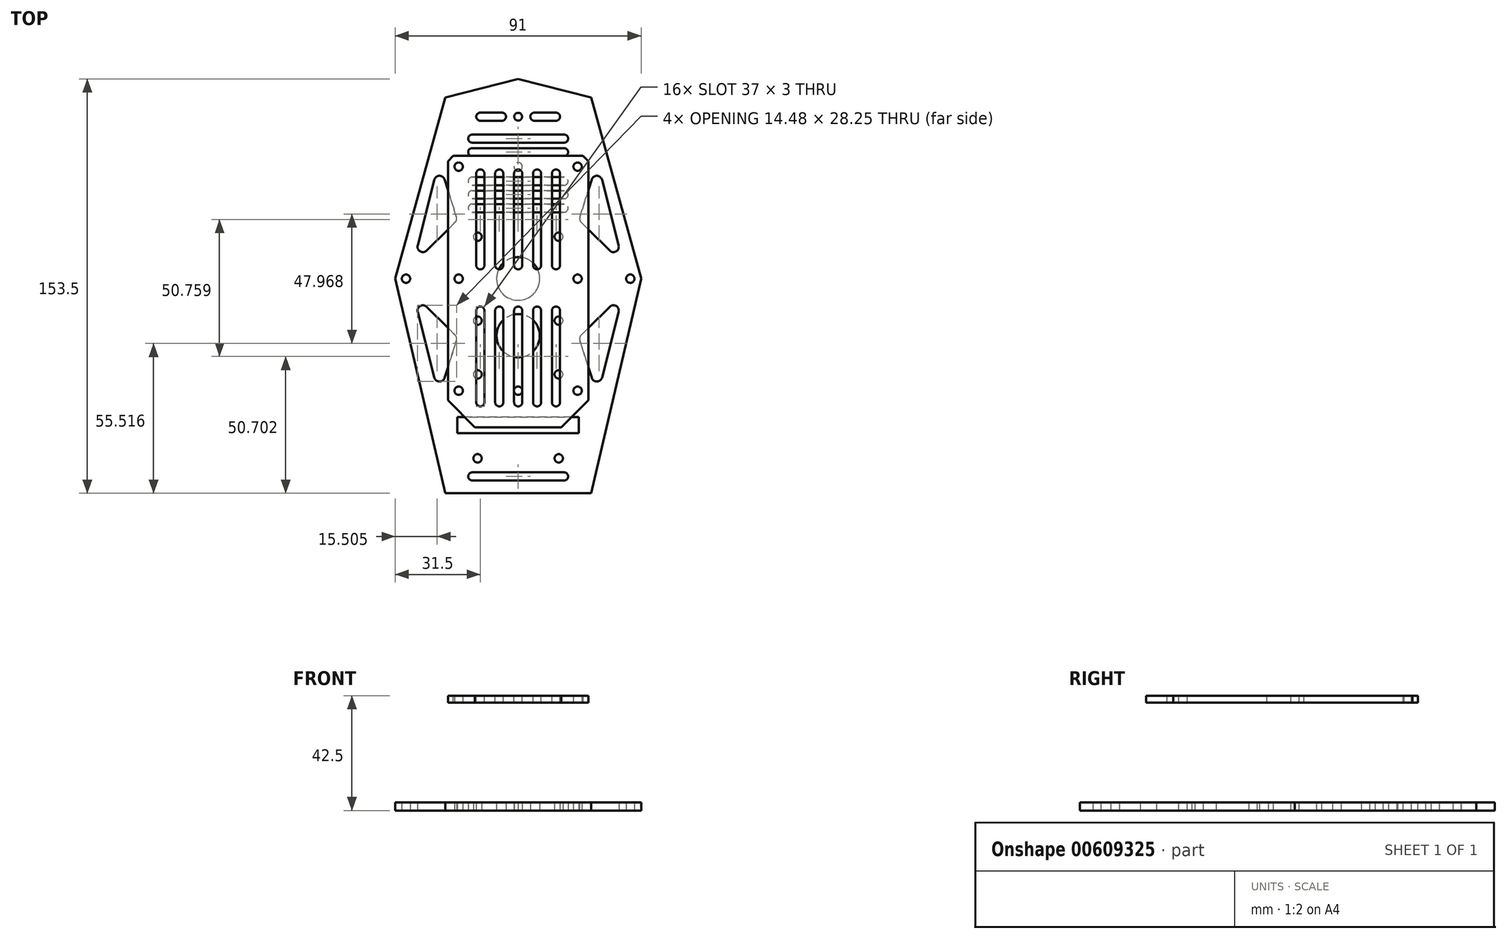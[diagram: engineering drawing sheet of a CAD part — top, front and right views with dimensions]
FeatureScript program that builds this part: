
annotation { "Feature Type Name" : "Feature", "Feature Type Description" : "" }
export const myFeature = defineFeature(function(context is Context, id is Id, definition is map)
    precondition{}
    {
        {
            var Q0;
            Q0=qCreatedBy(makeId("Top.planeOp"),FACE);
            var sketch = newSketch(context, id + "F0", { "sketchPlane" : qUnion([Q0])});
            skLineSegment(sketch, "E0", {"start": v(-27, 60) * mm, "end": v(27, 60) * mm, "construction": true});
            skLineSegment(sketch, "E1.MirrorCS", {"start": v(-27, -60) * mm, "end": v(27, -60) * mm, "construction": true});
            skCircle(sketch, "E2", {"center": v(0, 0) * mm, "radius": 8 * mm});
            skCircle(sketch, "E3", {"center": v(-41.5, 0) * mm, "radius": 1.55 * mm});
            skCircle(sketch, "E4.MirrorC", {"center": v(41.5, 0) * mm, "radius": 1.55 * mm});
            skCircle(sketch, "E5", {"center": v(0, 41.5) * mm, "radius": 1.55 * mm});
            skCircle(sketch, "E6.MirrorC", {"center": v(0, -41.5) * mm, "radius": 1.55 * mm});
            skCircle(sketch, "E7", {"center": v(0, 60) * mm, "radius": 1.46 * mm});
            skLineSegment(sketch, "E8", {"start": v(-6, 60) * mm, "end": v(-6, 61.5) * mm});
            skLineSegment(sketch, "E9", {"start": v(-6, 61.5) * mm, "end": v(-14, 61.5) * mm});
            skLineSegment(sketch, "E10", {"start": v(-14, 61.5) * mm, "end": v(-14, 58.5) * mm});
            skLineSegment(sketch, "E11", {"start": v(-14, 58.5) * mm, "end": v(-6, 58.5) * mm});
            skLineSegment(sketch, "E12", {"start": v(-6, 58.5) * mm, "end": v(-6, 60) * mm});
            skCircle(sketch, "E13", {"center": v(-6, 60) * mm, "radius": 1.5 * mm});
            skCircle(sketch, "E14", {"center": v(-14, 60) * mm, "radius": 1.5 * mm});
            skLineSegment(sketch, "E15.MirrorCS", {"start": v(6, 60) * mm, "end": v(6, 61.5) * mm});
            skLineSegment(sketch, "E16.MirrorCS", {"start": v(6, 58.5) * mm, "end": v(6, 60) * mm});
            skLineSegment(sketch, "E17.MirrorCS", {"start": v(14, 61.5) * mm, "end": v(14, 58.5) * mm});
            skCircle(sketch, "E18.MirrorC", {"center": v(6, 60) * mm, "radius": 1.5 * mm});
            skLineSegment(sketch, "E19.MirrorCS", {"start": v(14, 58.5) * mm, "end": v(6, 58.5) * mm});
            skCircle(sketch, "E20.MirrorC", {"center": v(14, 60) * mm, "radius": 1.5 * mm});
            skLineSegment(sketch, "E21.MirrorCS", {"start": v(6, 61.5) * mm, "end": v(14, 61.5) * mm});
            skSolve(sketch);
        }
        {
            var Q0;
            Q0=qCreatedBy(makeId("Top.planeOp"),FACE);
            var sketch = newSketch(context, id + "F1", { "sketchPlane" : qUnion([Q0])});
            skLineSegment(sketch, "E22.bottom", {"start": v(-18.5, 18.5) * mm, "end": v(18.5, 18.5) * mm, "construction": true});
            skLineSegment(sketch, "E22.top", {"start": v(-18.5, -18.5) * mm, "end": v(18.5, -18.5) * mm, "construction": true});
            skLineSegment(sketch, "E22.left", {"start": v(-18.5, 18.5) * mm, "end": v(-18.5, -18.5) * mm, "construction": true});
            skLineSegment(sketch, "E22.right", {"start": v(18.5, 18.5) * mm, "end": v(18.5, -18.5) * mm, "construction": true});
            skLineSegment(sketch, "E23.bottom", {"start": v(-15.02, 15.55) * mm, "end": v(15.02, 15.55) * mm, "construction": true});
            skLineSegment(sketch, "E23.top", {"start": v(-15.02, -15.55) * mm, "end": v(15.02, -15.55) * mm, "construction": true});
            skLineSegment(sketch, "E23.left", {"start": v(-15.02, 15.55) * mm, "end": v(-15.02, -15.55) * mm, "construction": true});
            skLineSegment(sketch, "E23.right", {"start": v(15.02, 15.55) * mm, "end": v(15.02, -15.55) * mm, "construction": true});
            skPoint(sketch, "E23.middle", {"position": v(0, 0) * mm});
            skCircle(sketch, "E24", {"center": v(-15.02, 15.55) * mm, "radius": 1.55 * mm});
            skCircle(sketch, "E25", {"center": v(-15.02, -15.55) * mm, "radius": 1.55 * mm});
            skCircle(sketch, "E26", {"center": v(15.02, -15.55) * mm, "radius": 1.55 * mm});
            skCircle(sketch, "E27", {"center": v(15.02, 15.55) * mm, "radius": 1.55 * mm});
            skLineSegment(sketch, "E28", {"start": v(0, -18.5) * mm, "end": v(0, -25.5) * mm, "construction": true});
            skLineSegment(sketch, "E29", {"start": v(0, -25.5) * mm, "end": v(18.5, -25.5) * mm, "construction": true});
            skCircle(sketch, "E30.MirrorC", {"center": v(-15.02, -66.55) * mm, "radius": 1.55 * mm});
            skCircle(sketch, "E31.MirrorC", {"center": v(-15.02, -35.45) * mm, "radius": 1.55 * mm});
            skCircle(sketch, "E32.MirrorC", {"center": v(15.02, -66.55) * mm, "radius": 1.55 * mm});
            skCircle(sketch, "E33.MirrorC", {"center": v(15.02, -35.45) * mm, "radius": 1.55 * mm});
            skLineSegment(sketch, "E34.MirrorCS", {"start": v(15.02, -66.55) * mm, "end": v(15.02, -35.45) * mm, "construction": true});
            skLineSegment(sketch, "E35.MirrorCS", {"start": v(-15.02, -66.55) * mm, "end": v(-15.02, -35.45) * mm, "construction": true});
            skLineSegment(sketch, "E36.MirrorCS", {"start": v(-15.02, -35.45) * mm, "end": v(15.02, -35.45) * mm, "construction": true});
            skLineSegment(sketch, "E37.MirrorCS", {"start": v(-15.02, -66.55) * mm, "end": v(15.02, -66.55) * mm, "construction": true});
            skLineSegment(sketch, "E38.MirrorCS", {"start": v(18.5, -69.5) * mm, "end": v(18.5, -32.5) * mm, "construction": true});
            skLineSegment(sketch, "E39.MirrorCS", {"start": v(-18.5, -69.5) * mm, "end": v(-18.5, -32.5) * mm, "construction": true});
            skLineSegment(sketch, "E40.MirrorCS", {"start": v(-18.5, -32.5) * mm, "end": v(18.5, -32.5) * mm, "construction": true});
            skPoint(sketch, "E41.MirrorP", {"position": v(0, -51) * mm});
            skLineSegment(sketch, "E42.MirrorCS", {"start": v(-18.5, -69.5) * mm, "end": v(18.5, -69.5) * mm, "construction": true});
            skLineSegment(sketch, "E43.bottom", {"start": v(-22.5, -57.25) * mm, "end": v(22.5, -57.25) * mm});
            skLineSegment(sketch, "E43.top", {"start": v(-22.5, -51.25) * mm, "end": v(22.5, -51.25) * mm});
            skLineSegment(sketch, "E43.left", {"start": v(-22.5, -57.25) * mm, "end": v(-22.5, -51.25) * mm});
            skLineSegment(sketch, "E43.right", {"start": v(22.5, -57.25) * mm, "end": v(22.5, -51.25) * mm});
            skPoint(sketch, "E43.middle", {"position": v(0, -54.25) * mm});
            skSolve(sketch);
        }
        {
            var Q0;
            Q0=qCreatedBy(makeId("Top.planeOp"),FACE);
            var sketch = newSketch(context, id + "F2", { "sketchPlane" : qUnion([Q0])});
            skLineSegment(sketch, "E44", {"start": v(-27, 67.16) * mm, "end": v(-45.5, 0) * mm});
            skLineSegment(sketch, "E45", {"start": v(-45.5, 0) * mm, "end": v(-27, -79.5) * mm});
            skLineSegment(sketch, "E46", {"start": v(-27, -79.5) * mm, "end": v(0, -79.5) * mm});
            skLineSegment(sketch, "E47.MirrorCS", {"start": v(27, 67.16) * mm, "end": v(45.5, 0) * mm});
            skLineSegment(sketch, "E48.MirrorCS", {"start": v(45.5, 0) * mm, "end": v(27, -79.5) * mm});
            skLineSegment(sketch, "E49.MirrorCS", {"start": v(27, -79.5) * mm, "end": v(0, -79.5) * mm});
            skPoint(sketch, "E50.0", {"position": v(-41.5, 0) * mm});
            skPoint(sketch, "E51.0", {"position": v(0, 60) * mm});
            skLineSegment(sketch, "E52", {"start": v(-27, 67.16) * mm, "end": v(0, 74) * mm});
            skLineSegment(sketch, "E53", {"start": v(0, 74) * mm, "end": v(27, 67.16) * mm});
            skPoint(sketch, "E54.0", {"position": v(0, -69.5) * mm});
            skSolve(sketch);
        }
        {
            var Q0;
            Q0 = qSketchRegion(id + "F2", true);
            extrude(context, id + "F3", {"entities" : qUnion([Q0]), "depth" : 3 * mm, "offsetDistance" : 25 * mm});
        }
        {
            var Q0;
            Q0 = qSketchRegion(id + "F0", true);
            extrude(context, id + "F4", {"entities" : qUnion([Q0]), "operationType" : NewBodyOperationType.REMOVE, "depth" : 25 * mm, "offsetDistance" : 25 * mm, "hasSecondDirection" : true, "secondDirectionOppositeDirection" : true, "secondDirectionDepth" : 25 * mm});
        }
        {
            var Q0;
            Q0 = qSketchRegion(id + "F1", true);
            extrude(context, id + "F5", {"entities" : qUnion([Q0]), "operationType" : NewBodyOperationType.REMOVE, "depth" : 25 * mm, "offsetDistance" : 25 * mm});
        }
        {
            var Q0;
            Q0=qCreatedBy(makeId("Top.planeOp"),FACE);
            var sketch = newSketch(context, id + "F6", { "sketchPlane" : qUnion([Q0])});
            skLineSegment(sketch, "E55", {"start": v(-31.05, -36.6) * mm, "end": v(-37.18, -12.33) * mm});
            skLineSegment(sketch, "E56", {"start": v(-33.83, -10.43) * mm, "end": v(-23.34, -20.85) * mm});
            skLineSegment(sketch, "E57", {"start": v(-22.85, -22.87) * mm, "end": v(-27.2, -36.7) * mm});
            skPoint(sketch, "E58.visualSharp", {"position": v(-38.95, -5.34) * mm});
            skArc(sketch, "E58.filletArc", {"start": v(-33.83, -10.43) * mm, "mid": v(-36.23, -10.1) * mm, "end": v(-37.18, -12.33) * mm});
            skPoint(sketch, "E59.visualSharp", {"position": v(-22.48, -21.7) * mm});
            skArc(sketch, "E59.filletArc", {"start": v(-22.85, -22.87) * mm, "mid": v(-22.81, -21.8) * mm, "end": v(-23.34, -20.85) * mm});
            skPoint(sketch, "E60.visualSharp", {"position": v(-29.32, -43.44) * mm});
            skArc(sketch, "E60.filletArc", {"start": v(-31.05, -36.6) * mm, "mid": v(-29.17, -38.1) * mm, "end": v(-27.2, -36.7) * mm});
            skArc(sketch, "E61.MirrorCS", {"start": v(-22.85, 22.87) * mm, "mid": v(-22.81, 21.8) * mm, "end": v(-23.34, 20.85) * mm});
            skArc(sketch, "E62.MirrorCS", {"start": v(-31.05, 36.6) * mm, "mid": v(-29.17, 38.1) * mm, "end": v(-27.2, 36.7) * mm});
            skArc(sketch, "E63.MirrorCS", {"start": v(-33.83, 10.43) * mm, "mid": v(-36.23, 10.1) * mm, "end": v(-37.18, 12.33) * mm});
            skLineSegment(sketch, "E64.MirrorCS", {"start": v(-33.83, 10.43) * mm, "end": v(-23.34, 20.85) * mm});
            skLineSegment(sketch, "E65.MirrorCS", {"start": v(-22.85, 22.87) * mm, "end": v(-27.2, 36.7) * mm});
            skLineSegment(sketch, "E66.MirrorCS", {"start": v(-31.05, 36.6) * mm, "end": v(-37.18, 12.33) * mm});
            skPoint(sketch, "E67.MirrorP", {"position": v(-22.48, 21.7) * mm});
            skArc(sketch, "E68.MirrorCS", {"start": v(22.85, 22.87) * mm, "mid": v(22.81, 21.8) * mm, "end": v(23.34, 20.85) * mm});
            skArc(sketch, "E69.MirrorCS", {"start": v(31.05, 36.6) * mm, "mid": v(29.17, 38.1) * mm, "end": v(27.2, 36.7) * mm});
            skLineSegment(sketch, "E70.MirrorCS", {"start": v(31.05, 36.6) * mm, "end": v(37.18, 12.33) * mm});
            skArc(sketch, "E71.MirrorCS", {"start": v(33.83, 10.43) * mm, "mid": v(36.23, 10.1) * mm, "end": v(37.18, 12.33) * mm});
            skLineSegment(sketch, "E72.MirrorCS", {"start": v(33.83, 10.43) * mm, "end": v(23.34, 20.85) * mm});
            skLineSegment(sketch, "E73.MirrorCS", {"start": v(22.85, 22.87) * mm, "end": v(27.2, 36.7) * mm});
            skArc(sketch, "E74.MirrorCS", {"start": v(22.85, -22.87) * mm, "mid": v(22.81, -21.8) * mm, "end": v(23.34, -20.85) * mm});
            skArc(sketch, "E75.MirrorCS", {"start": v(31.05, -36.6) * mm, "mid": v(29.17, -38.1) * mm, "end": v(27.2, -36.7) * mm});
            skArc(sketch, "E76.MirrorCS", {"start": v(33.83, -10.43) * mm, "mid": v(36.23, -10.1) * mm, "end": v(37.18, -12.33) * mm});
            skPoint(sketch, "E77.MirrorP", {"position": v(22.48, -21.7) * mm});
            skLineSegment(sketch, "E78.MirrorCS", {"start": v(22.85, -22.87) * mm, "end": v(27.2, -36.7) * mm});
            skLineSegment(sketch, "E79.MirrorCS", {"start": v(33.83, -10.43) * mm, "end": v(23.34, -20.85) * mm});
            skLineSegment(sketch, "E80.MirrorCS", {"start": v(31.05, -36.6) * mm, "end": v(37.18, -12.33) * mm});
            skPoint(sketch, "E81.MirrorP", {"position": v(29.32, -43.44) * mm});
            skPoint(sketch, "E82.MirrorP", {"position": v(38.95, -5.34) * mm});
            skLineSegment(sketch, "E83.bottom", {"start": v(-17, 24.62) * mm, "end": v(17, 24.62) * mm});
            skLineSegment(sketch, "E83.top", {"start": v(-17, 27.62) * mm, "end": v(17, 27.62) * mm});
            skLineSegment(sketch, "E83.left", {"start": v(-18.5, 26.12) * mm, "end": v(-18.5, 26.12) * mm});
            skLineSegment(sketch, "E83.right", {"start": v(18.5, 26.12) * mm, "end": v(18.5, 26.12) * mm});
            skPoint(sketch, "E83.middle", {"position": v(0, 26.12) * mm});
            skPoint(sketch, "E84.visualSharp", {"position": v(-18.5, 24.62) * mm});
            skArc(sketch, "E84.filletArc", {"start": v(-18.5, 26.12) * mm, "mid": v(-18.06, 25.06) * mm, "end": v(-17, 24.62) * mm});
            skPoint(sketch, "E85.visualSharp", {"position": v(-18.5, 27.62) * mm});
            skArc(sketch, "E85.filletArc", {"start": v(-17, 27.62) * mm, "mid": v(-18.06, 27.18) * mm, "end": v(-18.5, 26.12) * mm});
            skPoint(sketch, "E86.visualSharp", {"position": v(18.5, 27.62) * mm});
            skArc(sketch, "E86.filletArc", {"start": v(18.5, 26.12) * mm, "mid": v(18.06, 27.18) * mm, "end": v(17, 27.62) * mm});
            skPoint(sketch, "E87.visualSharp", {"position": v(18.5, 24.62) * mm});
            skArc(sketch, "E87.filletArc", {"start": v(17, 24.62) * mm, "mid": v(18.06, 25.06) * mm, "end": v(18.5, 26.12) * mm});
            skPoint(sketch, "E88.0.1.0", {"position": v(-18.5, 29.62) * mm});
            skPoint(sketch, "E88.0.1.1", {"position": v(18.5, 32.62) * mm});
            skLineSegment(sketch, "E88.0.1.2", {"start": v(-17, 29.62) * mm, "end": v(17, 29.62) * mm});
            skPoint(sketch, "E88.0.1.3", {"position": v(0, 31.12) * mm});
            skPoint(sketch, "E88.0.1.4", {"position": v(18.5, 29.62) * mm});
            skPoint(sketch, "E88.0.1.5", {"position": v(-18.5, 32.62) * mm});
            skLineSegment(sketch, "E88.0.1.6", {"start": v(-17, 32.62) * mm, "end": v(17, 32.62) * mm});
            skArc(sketch, "E88.0.1.7", {"start": v(18.5, 31.12) * mm, "mid": v(18.06, 32.18) * mm, "end": v(17, 32.62) * mm});
            skArc(sketch, "E88.0.1.8", {"start": v(-17, 32.62) * mm, "mid": v(-18.06, 32.18) * mm, "end": v(-18.5, 31.12) * mm});
            skArc(sketch, "E88.0.1.9", {"start": v(17, 29.62) * mm, "mid": v(18.06, 30.06) * mm, "end": v(18.5, 31.12) * mm});
            skArc(sketch, "E88.0.1.10", {"start": v(-18.5, 31.12) * mm, "mid": v(-18.06, 30.06) * mm, "end": v(-17, 29.62) * mm});
            skPoint(sketch, "E88.0.2.0", {"position": v(-18.5, 34.62) * mm});
            skPoint(sketch, "E88.0.2.1", {"position": v(18.5, 37.62) * mm});
            skLineSegment(sketch, "E88.0.2.2", {"start": v(-17, 34.62) * mm, "end": v(17, 34.62) * mm});
            skPoint(sketch, "E88.0.2.3", {"position": v(0, 36.12) * mm});
            skPoint(sketch, "E88.0.2.4", {"position": v(18.5, 34.62) * mm});
            skPoint(sketch, "E88.0.2.5", {"position": v(-18.5, 37.62) * mm});
            skLineSegment(sketch, "E88.0.2.6", {"start": v(-17, 37.62) * mm, "end": v(17, 37.62) * mm});
            skArc(sketch, "E88.0.2.7", {"start": v(18.5, 36.12) * mm, "mid": v(18.06, 37.18) * mm, "end": v(17, 37.62) * mm});
            skArc(sketch, "E88.0.2.8", {"start": v(-17, 37.62) * mm, "mid": v(-18.06, 37.18) * mm, "end": v(-18.5, 36.12) * mm});
            skArc(sketch, "E88.0.2.9", {"start": v(17, 34.62) * mm, "mid": v(18.06, 35.06) * mm, "end": v(18.5, 36.12) * mm});
            skArc(sketch, "E88.0.2.10", {"start": v(-18.5, 36.12) * mm, "mid": v(-18.06, 35.06) * mm, "end": v(-17, 34.62) * mm});
            skLineSegment(sketch, "E88.direction1", {"start": v(-18.5, 24.62) * mm, "end": v(11.1, 24.62) * mm, "construction": true});
            skLineSegment(sketch, "E88.direction2", {"start": v(-18.5, 24.62) * mm, "end": v(-18.5, 29.62) * mm, "construction": true});
            skPoint(sketch, "E89.0", {"position": v(0, 41.5) * mm});
            skLineSegment(sketch, "E90", {"start": v(0, 41.5) * mm, "end": v(16.84, 41.5) * mm});
            skArc(sketch, "E91.MirrorCS", {"start": v(18.5, 46.88) * mm, "mid": v(18.06, 45.82) * mm, "end": v(17, 45.38) * mm});
            skArc(sketch, "E92.MirrorCS", {"start": v(18.5, 51.88) * mm, "mid": v(18.06, 50.82) * mm, "end": v(17, 50.38) * mm});
            skArc(sketch, "E93.MirrorCS", {"start": v(-17, 45.38) * mm, "mid": v(-18.06, 45.82) * mm, "end": v(-18.5, 46.88) * mm});
            skArc(sketch, "E94.MirrorCS", {"start": v(-18.5, 46.88) * mm, "mid": v(-18.06, 47.94) * mm, "end": v(-17, 48.38) * mm});
            skArc(sketch, "E95.MirrorCS", {"start": v(17, 53.38) * mm, "mid": v(18.06, 52.94) * mm, "end": v(18.5, 51.88) * mm});
            skArc(sketch, "E96.MirrorCS", {"start": v(17, 48.38) * mm, "mid": v(18.06, 47.94) * mm, "end": v(18.5, 46.88) * mm});
            skArc(sketch, "E97.MirrorCS", {"start": v(-17, 50.38) * mm, "mid": v(-18.06, 50.82) * mm, "end": v(-18.5, 51.88) * mm});
            skArc(sketch, "E98.MirrorCS", {"start": v(-18.5, 51.88) * mm, "mid": v(-18.06, 52.94) * mm, "end": v(-17, 53.38) * mm});
            skPoint(sketch, "E99.MirrorP", {"position": v(-18.5, 55.38) * mm});
            skPoint(sketch, "E100.MirrorP", {"position": v(18.5, 55.38) * mm});
            skLineSegment(sketch, "E101.MirrorCS", {"start": v(-17, 50.38) * mm, "end": v(17, 50.38) * mm});
            skPoint(sketch, "E102.MirrorP", {"position": v(18.5, 50.38) * mm});
            skLineSegment(sketch, "E103.MirrorCS", {"start": v(-17, 48.38) * mm, "end": v(17, 48.38) * mm});
            skPoint(sketch, "E104.MirrorP", {"position": v(18.5, 45.38) * mm});
            skPoint(sketch, "E105.MirrorP", {"position": v(0, 51.88) * mm});
            skPoint(sketch, "E106.MirrorP", {"position": v(-18.5, 48.38) * mm});
            skPoint(sketch, "E107.MirrorP", {"position": v(-18.5, 53.38) * mm});
            skPoint(sketch, "E108.MirrorP", {"position": v(18.5, 48.38) * mm});
            skLineSegment(sketch, "E109.MirrorCS", {"start": v(-17, 45.38) * mm, "end": v(17, 45.38) * mm});
            skLineSegment(sketch, "E110.MirrorCS", {"start": v(-17, 53.38) * mm, "end": v(17, 53.38) * mm});
            skPoint(sketch, "E111.MirrorP", {"position": v(18.5, 53.38) * mm});
            skPoint(sketch, "E112.MirrorP", {"position": v(-18.5, 45.38) * mm});
            skPoint(sketch, "E113.MirrorP", {"position": v(-18.5, 50.38) * mm});
            skPoint(sketch, "E114.MirrorP", {"position": v(0, 46.88) * mm});
            skCircle(sketch, "E115", {"center": v(0, -21.12) * mm, "radius": 8 * mm});
            skLineSegment(sketch, "E116.bottom", {"start": v(17, -74.74) * mm, "end": v(-17, -74.74) * mm});
            skLineSegment(sketch, "E116.top", {"start": v(17, -71.74) * mm, "end": v(-17, -71.74) * mm});
            skLineSegment(sketch, "E116.left", {"start": v(18.5, -69.94) * mm, "end": v(18.5, -69.94) * mm});
            skLineSegment(sketch, "E116.right", {"start": v(-18.5, -69.94) * mm, "end": v(-18.5, -69.94) * mm});
            skPoint(sketch, "E116.middle", {"position": v(0, -73.24) * mm});
            skPoint(sketch, "E117.visualSharp", {"position": v(18.5, -71.74) * mm});
            skArc(sketch, "E117.filletArc", {"start": v(18.5, -73.24) * mm, "mid": v(18.06, -72.18) * mm, "end": v(17, -71.74) * mm});
            skPoint(sketch, "E118.visualSharp", {"position": v(18.5, -74.74) * mm});
            skArc(sketch, "E118.filletArc", {"start": v(17, -74.74) * mm, "mid": v(18.06, -74.3) * mm, "end": v(18.5, -73.24) * mm});
            skPoint(sketch, "E119.visualSharp", {"position": v(-18.5, -74.74) * mm});
            skArc(sketch, "E119.filletArc", {"start": v(-18.5, -73.24) * mm, "mid": v(-18.06, -74.3) * mm, "end": v(-17, -74.74) * mm});
            skPoint(sketch, "E120.visualSharp", {"position": v(-18.5, -71.74) * mm});
            skArc(sketch, "E120.filletArc", {"start": v(-17, -71.74) * mm, "mid": v(-18.06, -72.18) * mm, "end": v(-18.5, -73.24) * mm});
            skSolve(sketch);
        }
        {
            var Q0;
            Q0 = qSketchRegion(id + "F6", true);
            extrude(context, id + "F7", {"entities" : qUnion([Q0]), "operationType" : NewBodyOperationType.REMOVE, "depth" : 25 * mm, "offsetDistance" : 25 * mm});
        }
        {
            var Q0;
            Q0=makeQuery(id+"F3.opExtrude","CAP_FACE",FACE,{"disambiguationData":[OSD([sQuery(id+"F2.wireOp",EDGE,"E44"),sQuery(id+"F2.wireOp",EDGE,"E45"),sQuery(id+"F2.wireOp",EDGE,"E46"),sQuery(id+"F2.wireOp",EDGE,"E47.MirrorCS"),sQuery(id+"F2.wireOp",EDGE,"E48.MirrorCS"),sQuery(id+"F2.wireOp",EDGE,"E49.MirrorCS"),sQuery(id+"F2.wireOp",EDGE,"E52"),sQuery(id+"F2.wireOp",EDGE,"E53")])],"isStart":false});
            cPlane(context, id + "F8", {"entities" : qUnion([Q0]), "cplaneType" : CPlaneType.OFFSET, "offset" : 37 * mm, "width" : 150 * mm, "height" : 150 * mm});
        }
        {
            var Q0;
            Q0=qCreatedBy(id+"F8.planeOp",FACE);
            var sketch = newSketch(context, id + "F9", { "sketchPlane" : qUnion([Q0])});
            skLineSegment(sketch, "E121", {"start": v(0, 45.5) * mm, "end": v(-26, 45.5) * mm});
            skLineSegment(sketch, "E122", {"start": v(-26, 45.5) * mm, "end": v(-26, -55.02) * mm});
            skLineSegment(sketch, "E123", {"start": v(-26, -55.02) * mm, "end": v(0, -55.02) * mm});
            skLineSegment(sketch, "E124.MirrorCS", {"start": v(0, 45.5) * mm, "end": v(26, 45.5) * mm});
            skLineSegment(sketch, "E125.MirrorCS", {"start": v(26, 45.5) * mm, "end": v(26, -55.02) * mm});
            skLineSegment(sketch, "E126.MirrorCS", {"start": v(26, -55.02) * mm, "end": v(0, -55.02) * mm});
            skSolve(sketch);
        }
        {
            var Q0;
            Q0 = qSketchRegion(id + "F9", true);
            extrude(context, id + "F10", {"entities" : qUnion([Q0]), "depth" : 2.5 * mm, "offsetDistance" : 25 * mm});
        }
        {
            var Q0;
            Q0=qCreatedBy(makeId("Top.planeOp"),FACE);
            var sketch = newSketch(context, id + "F11", { "sketchPlane" : qUnion([Q0])});
            skPoint(sketch, "E127.0", {"position": v(0, 41.5) * mm});
            skCircle(sketch, "E128", {"center": v(-22, 41.5) * mm, "radius": 1.55 * mm});
            skPoint(sketch, "E129.0", {"position": v(0, 0) * mm});
            skCircle(sketch, "E130", {"center": v(-22, 0) * mm, "radius": 1.55 * mm});
            skPoint(sketch, "E131.0", {"position": v(0, -41.5) * mm});
            skCircle(sketch, "E132", {"center": v(-22, -41.5) * mm, "radius": 1.55 * mm});
            skCircle(sketch, "E133.MirrorC", {"center": v(22, 41.5) * mm, "radius": 1.55 * mm});
            skCircle(sketch, "E134.MirrorC", {"center": v(22, 0) * mm, "radius": 1.55 * mm});
            skCircle(sketch, "E135.MirrorC", {"center": v(22, -41.5) * mm, "radius": 1.55 * mm});
            skPoint(sketch, "E136.0", {"position": v(0, 37.35) * mm});
            skPoint(sketch, "E137.0", {"position": v(0, -4.15) * mm});
            skPoint(sketch, "E138.0", {"position": v(0, -45.65) * mm});
            skSolve(sketch);
        }
        {
            var Q0;
            Q0 = qSketchRegion(id + "F11", true);
            extrude(context, id + "F12", {"entities" : qUnion([Q0]), "operationType" : NewBodyOperationType.REMOVE, "depth" : 75 * mm, "offsetDistance" : 25 * mm});
        }
        {
            var Q0;
            Q0=makeQuery(id+"F10.opExtrude","CAP_FACE",FACE,{"disambiguationData":[OSD([sQuery(id+"F9.wireOp",EDGE,"E121"),sQuery(id+"F9.wireOp",EDGE,"E122"),sQuery(id+"F9.wireOp",EDGE,"E123"),sQuery(id+"F9.wireOp",EDGE,"E124.MirrorCS"),sQuery(id+"F9.wireOp",EDGE,"E125.MirrorCS"),sQuery(id+"F9.wireOp",EDGE,"E126.MirrorCS")])],"isStart":false});
            var sketch = newSketch(context, id + "F13", { "sketchPlane" : qUnion([Q0])});
            skLineSegment(sketch, "E139.bottom", {"start": v(1.5, 4.96) * mm, "end": v(-1.5, 4.96) * mm});
            skLineSegment(sketch, "E139.top", {"start": v(1.5, 38.96) * mm, "end": v(-1.5, 38.96) * mm});
            skLineSegment(sketch, "E139.left", {"start": v(1.5, 4.96) * mm, "end": v(1.5, 38.96) * mm});
            skLineSegment(sketch, "E139.right", {"start": v(-1.5, 4.96) * mm, "end": v(-1.5, 38.96) * mm});
            skPoint(sketch, "E139.middle", {"position": v(0, 21.96) * mm});
            skLineSegment(sketch, "E140.bottom", {"start": v(1.5, -45.8) * mm, "end": v(-1.5, -45.8) * mm});
            skLineSegment(sketch, "E140.top", {"start": v(1.5, -11.8) * mm, "end": v(-1.5, -11.8) * mm});
            skLineSegment(sketch, "E140.left", {"start": v(1.5, -45.8) * mm, "end": v(1.5, -11.8) * mm});
            skLineSegment(sketch, "E140.right", {"start": v(-1.5, -45.8) * mm, "end": v(-1.5, -11.8) * mm});
            skPoint(sketch, "E140.middle", {"position": v(0, -28.8) * mm});
            skPoint(sketch, "E140.middle.positionSnap0", {"position": v(0, 4.96) * mm});
            skPoint(sketch, "E140.centerSnap0", {"position": v(0, 4.96) * mm});
            skCircle(sketch, "E141", {"center": v(0, -11.8) * mm, "radius": 1.5 * mm});
            skCircle(sketch, "E142", {"center": v(0, 4.96) * mm, "radius": 1.5 * mm});
            skCircle(sketch, "E143", {"center": v(0, -45.8) * mm, "radius": 1.5 * mm});
            skCircle(sketch, "E144", {"center": v(0, 38.96) * mm, "radius": 1.5 * mm});
            skPoint(sketch, "E145.1.0.0", {"position": v(7, 4.96) * mm});
            skCircle(sketch, "E145.1.0.1", {"center": v(7, -11.8) * mm, "radius": 1.5 * mm});
            skCircle(sketch, "E145.1.0.2", {"center": v(7, -45.8) * mm, "radius": 1.5 * mm});
            skPoint(sketch, "E145.1.0.3", {"position": v(7, -28.8) * mm});
            skPoint(sketch, "E145.1.0.4", {"position": v(7, 21.96) * mm});
            skLineSegment(sketch, "E145.1.0.5", {"start": v(5.5, 4.96) * mm, "end": v(5.5, 38.96) * mm});
            skLineSegment(sketch, "E145.1.0.6", {"start": v(5.5, -45.8) * mm, "end": v(5.5, -11.8) * mm});
            skLineSegment(sketch, "E145.1.0.7", {"start": v(8.5, -45.8) * mm, "end": v(8.5, -11.8) * mm});
            skLineSegment(sketch, "E145.1.0.8", {"start": v(8.5, 4.96) * mm, "end": v(8.5, 38.96) * mm});
            skPoint(sketch, "E145.1.0.9", {"position": v(7, 4.96) * mm});
            skCircle(sketch, "E145.1.0.10", {"center": v(7, 38.96) * mm, "radius": 1.5 * mm});
            skCircle(sketch, "E145.1.0.11", {"center": v(7, 4.96) * mm, "radius": 1.5 * mm});
            skLineSegment(sketch, "E145.1.0.12", {"start": v(8.5, 38.96) * mm, "end": v(5.5, 38.96) * mm});
            skLineSegment(sketch, "E145.1.0.13", {"start": v(8.5, -45.8) * mm, "end": v(5.5, -45.8) * mm});
            skLineSegment(sketch, "E145.1.0.14", {"start": v(8.5, -11.8) * mm, "end": v(5.5, -11.8) * mm});
            skLineSegment(sketch, "E145.1.0.15", {"start": v(8.5, 4.96) * mm, "end": v(5.5, 4.96) * mm});
            skPoint(sketch, "E145.2.0.0", {"position": v(14, 4.96) * mm});
            skCircle(sketch, "E145.2.0.1", {"center": v(14, -11.8) * mm, "radius": 1.5 * mm});
            skCircle(sketch, "E145.2.0.2", {"center": v(14, -45.8) * mm, "radius": 1.5 * mm});
            skPoint(sketch, "E145.2.0.3", {"position": v(14, -28.8) * mm});
            skPoint(sketch, "E145.2.0.4", {"position": v(14, 21.96) * mm});
            skLineSegment(sketch, "E145.2.0.5", {"start": v(12.5, 4.96) * mm, "end": v(12.5, 38.96) * mm});
            skLineSegment(sketch, "E145.2.0.6", {"start": v(12.5, -45.8) * mm, "end": v(12.5, -11.8) * mm});
            skLineSegment(sketch, "E145.2.0.7", {"start": v(15.5, -45.8) * mm, "end": v(15.5, -11.8) * mm});
            skLineSegment(sketch, "E145.2.0.8", {"start": v(15.5, 4.96) * mm, "end": v(15.5, 38.96) * mm});
            skPoint(sketch, "E145.2.0.9", {"position": v(14, 4.96) * mm});
            skCircle(sketch, "E145.2.0.10", {"center": v(14, 38.96) * mm, "radius": 1.5 * mm});
            skCircle(sketch, "E145.2.0.11", {"center": v(14, 4.96) * mm, "radius": 1.5 * mm});
            skLineSegment(sketch, "E145.2.0.12", {"start": v(15.5, 38.96) * mm, "end": v(12.5, 38.96) * mm});
            skLineSegment(sketch, "E145.2.0.13", {"start": v(15.5, -45.8) * mm, "end": v(12.5, -45.8) * mm});
            skLineSegment(sketch, "E145.2.0.14", {"start": v(15.5, -11.8) * mm, "end": v(12.5, -11.8) * mm});
            skLineSegment(sketch, "E145.2.0.15", {"start": v(15.5, 4.96) * mm, "end": v(12.5, 4.96) * mm});
            skLineSegment(sketch, "E145.direction1", {"start": v(-1.5, -45.8) * mm, "end": v(5.5, -45.8) * mm, "construction": true});
            skCircle(sketch, "E146.1.0.0", {"center": v(-7, -45.8) * mm, "radius": 1.5 * mm});
            skPoint(sketch, "E146.1.0.1", {"position": v(-7, -28.8) * mm});
            skLineSegment(sketch, "E146.1.0.2", {"start": v(-5.5, 4.96) * mm, "end": v(-5.5, 38.96) * mm});
            skLineSegment(sketch, "E146.1.0.3", {"start": v(-8.5, -45.8) * mm, "end": v(-8.5, -11.8) * mm});
            skCircle(sketch, "E146.1.0.4", {"center": v(-7, -11.8) * mm, "radius": 1.5 * mm});
            skCircle(sketch, "E146.1.0.5", {"center": v(-7, 38.96) * mm, "radius": 1.5 * mm});
            skPoint(sketch, "E146.1.0.6", {"position": v(-7, 21.96) * mm});
            skLineSegment(sketch, "E146.1.0.7", {"start": v(-8.5, 4.96) * mm, "end": v(-8.5, 38.96) * mm});
            skLineSegment(sketch, "E146.1.0.8", {"start": v(-5.5, -45.8) * mm, "end": v(-5.5, -11.8) * mm});
            skPoint(sketch, "E146.1.0.9", {"position": v(-7, 4.96) * mm});
            skPoint(sketch, "E146.1.0.10", {"position": v(-7, 4.96) * mm});
            skCircle(sketch, "E146.1.0.11", {"center": v(-7, 4.96) * mm, "radius": 1.5 * mm});
            skLineSegment(sketch, "E146.1.0.12", {"start": v(-5.5, -45.8) * mm, "end": v(-8.5, -45.8) * mm});
            skLineSegment(sketch, "E146.1.0.13", {"start": v(-5.5, -11.8) * mm, "end": v(-8.5, -11.8) * mm});
            skLineSegment(sketch, "E146.1.0.14", {"start": v(-5.5, 38.96) * mm, "end": v(-8.5, 38.96) * mm});
            skLineSegment(sketch, "E146.1.0.15", {"start": v(-5.5, 4.96) * mm, "end": v(-8.5, 4.96) * mm});
            skCircle(sketch, "E146.2.0.0", {"center": v(-14, -45.8) * mm, "radius": 1.5 * mm});
            skPoint(sketch, "E146.2.0.1", {"position": v(-14, -28.8) * mm});
            skLineSegment(sketch, "E146.2.0.2", {"start": v(-12.5, 4.96) * mm, "end": v(-12.5, 38.96) * mm});
            skLineSegment(sketch, "E146.2.0.3", {"start": v(-15.5, -45.8) * mm, "end": v(-15.5, -11.8) * mm});
            skCircle(sketch, "E146.2.0.4", {"center": v(-14, -11.8) * mm, "radius": 1.5 * mm});
            skCircle(sketch, "E146.2.0.5", {"center": v(-14, 38.96) * mm, "radius": 1.5 * mm});
            skPoint(sketch, "E146.2.0.6", {"position": v(-14, 21.96) * mm});
            skLineSegment(sketch, "E146.2.0.7", {"start": v(-15.5, 4.96) * mm, "end": v(-15.5, 38.96) * mm});
            skLineSegment(sketch, "E146.2.0.8", {"start": v(-12.5, -45.8) * mm, "end": v(-12.5, -11.8) * mm});
            skPoint(sketch, "E146.2.0.9", {"position": v(-14, 4.96) * mm});
            skPoint(sketch, "E146.2.0.10", {"position": v(-14, 4.96) * mm});
            skCircle(sketch, "E146.2.0.11", {"center": v(-14, 4.96) * mm, "radius": 1.5 * mm});
            skLineSegment(sketch, "E146.2.0.12", {"start": v(-12.5, -45.8) * mm, "end": v(-15.5, -45.8) * mm});
            skLineSegment(sketch, "E146.2.0.13", {"start": v(-12.5, -11.8) * mm, "end": v(-15.5, -11.8) * mm});
            skLineSegment(sketch, "E146.2.0.14", {"start": v(-12.5, 38.96) * mm, "end": v(-15.5, 38.96) * mm});
            skLineSegment(sketch, "E146.2.0.15", {"start": v(-12.5, 4.96) * mm, "end": v(-15.5, 4.96) * mm});
            skLineSegment(sketch, "E146.direction1", {"start": v(-1.5, -45.8) * mm, "end": v(-8.5, -45.8) * mm, "construction": true});
            skSolve(sketch);
        }
        {
            var Q0;
            Q0 = qSketchRegion(id + "F13", true);
            extrude(context, id + "F14", {"entities" : qUnion([Q0]), "operationType" : NewBodyOperationType.REMOVE, "oppositeDirection" : true, "depth" : 25 * mm, "offsetDistance" : 25 * mm});
        }
        {
            var Q0;
            Q0=makeQuery(id+"F10.opExtrude","SWEPT_EDGE",EDGE,{"disambiguationData":[OSD([sQuery(id+"F9.wireOp",EDGE,"E122"),sQuery(id+"F9.wireOp",EDGE,"E123")])]});
            var Q1;
            Q1=makeQuery(id+"F10.opExtrude","SWEPT_EDGE",EDGE,{"disambiguationData":[OSD([sQuery(id+"F9.wireOp",EDGE,"E125.MirrorCS"),sQuery(id+"F9.wireOp",EDGE,"E126.MirrorCS")])]});
            chamfer(context, id + "F15", {"entities" : qUnion([Q0, Q1]), "width" : 10 * mm, "tangentPropagation" : true});
        }
        {
            var Q0;
            Q0=makeQuery(id+"F10.opExtrude","SWEPT_EDGE",EDGE,{"disambiguationData":[OSD([sQuery(id+"F9.wireOp",EDGE,"E121"),sQuery(id+"F9.wireOp",EDGE,"E122")])]});
            var Q1;
            Q1=makeQuery(id+"F10.opExtrude","SWEPT_EDGE",EDGE,{"disambiguationData":[OSD([sQuery(id+"F9.wireOp",EDGE,"E124.MirrorCS"),sQuery(id+"F9.wireOp",EDGE,"E125.MirrorCS")])]});
            chamfer(context, id + "F16", {"entities" : qUnion([Q0, Q1]), "width" : 2 * mm, "tangentPropagation" : true});
        }
    });
